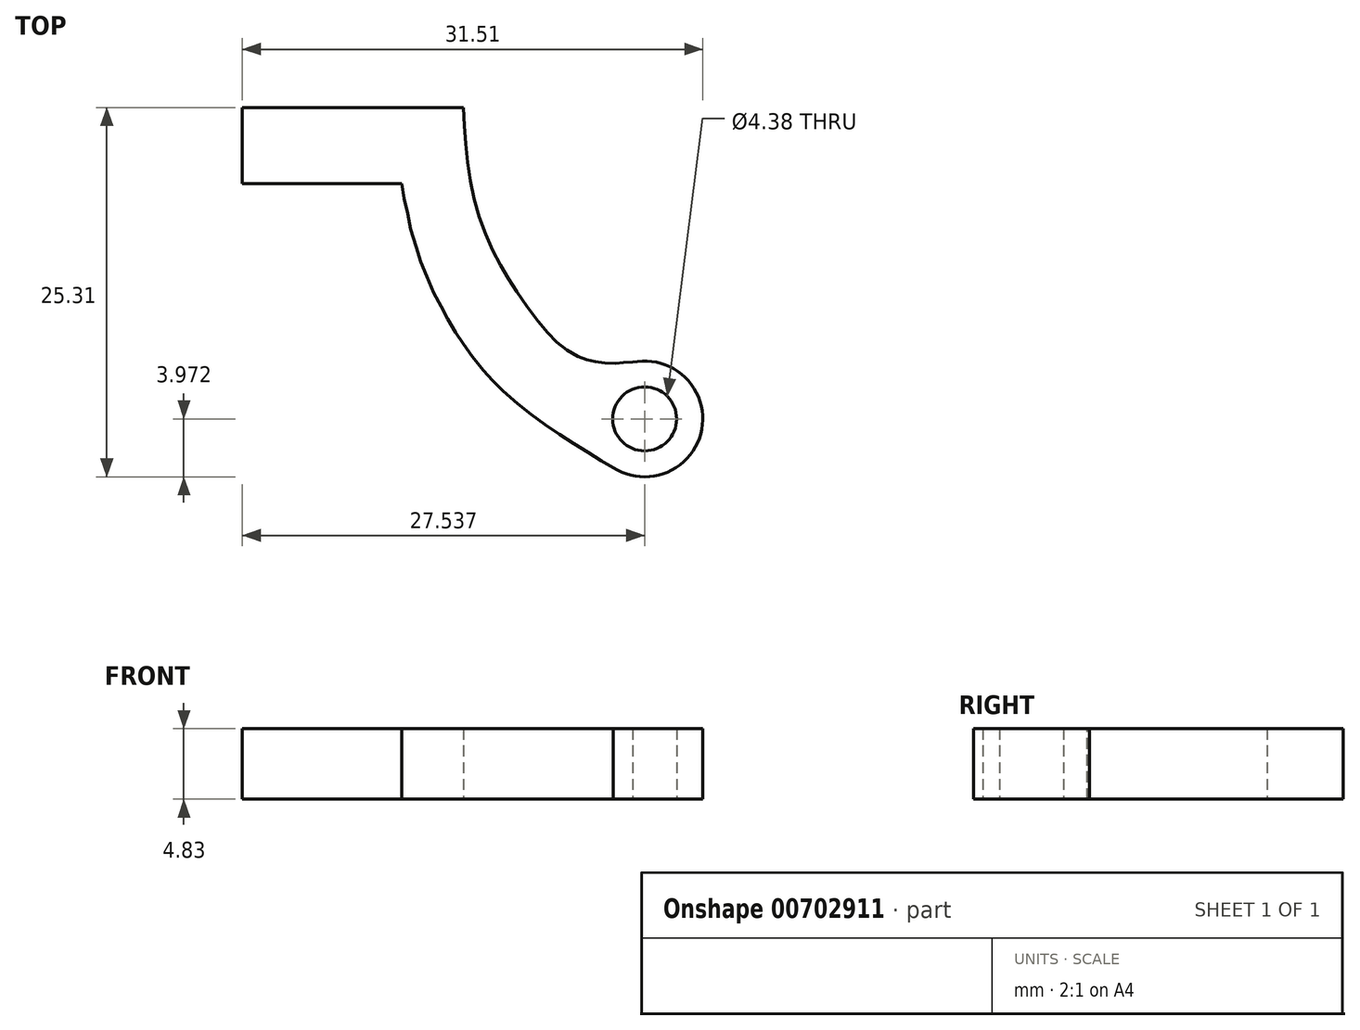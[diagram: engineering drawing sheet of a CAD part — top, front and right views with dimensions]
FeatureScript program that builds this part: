
annotation { "Feature Type Name" : "Feature", "Feature Type Description" : "" }
export const myFeature = defineFeature(function(context is Context, id is Id, definition is map)
    precondition{}
    {
        {
            var Q0;
            Q0=qCreatedBy(makeId("Top.planeOp"),FACE);
            var sketch = newSketch(context, id + "F0", { "sketchPlane" : qUnion([Q0])});
            skCircle(sketch, "E0", {"center": v(26.2, -11.99) * mm, "radius": 2.2 * mm});
            skArc(sketch, "E1", {"start": v(24.06, -15.33) * mm, "mid": v(30.11, -12.7) * mm, "end": v(25.38, -8.1) * mm});
            skLineSegment(sketch, "E2", {"start": v(-1.33, 9.35) * mm, "end": v(13.8, 9.35) * mm});
            skLineSegment(sketch, "E3", {"start": v(-1.33, 9.35) * mm, "end": v(-1.33, 4.13) * mm});
            skLineSegment(sketch, "E4", {"start": v(-1.33, 4.13) * mm, "end": v(9.6, 4.13) * mm});
            skFitSpline(sketch, "E5", {"points": [v(13.8, 9.35) * mm, v(13.95, 6.96) * mm, v(14.25, 4.44) * mm, v(14.82, 2.05) * mm, v(15.7, -0.2) * mm, v(16.6, -1.92) * mm, v(17.55, -3.41) * mm, v(18.98, -5.38) * mm, v(19.94, -6.46) * mm, v(20.8, -7.22) * mm, v(21.81, -7.78) * mm, v(22.31, -7.95) * mm, v(22.89, -8.08) * mm, v(23.6, -8.16) * mm, v(24.34, -8.18) * mm, v(24.75, -8.13) * mm, v(25.38, -8.1) * mm], "startDerivative": vector(1.35, -28.19) * mm, "endDerivative": vector(13.52, -1.17) * mm});
            skFitSpline(sketch, "E6", {"points": [v(9.6, 4.13) * mm, v(9.73, 3.17) * mm, v(9.97, 2.13) * mm, v(10.16, 1.16) * mm, v(10.57, -0.23) * mm, v(10.89, -1.25) * mm, v(11.3, -2.28) * mm, v(11.85, -3.52) * mm, v(12.32, -4.39) * mm, v(12.73, -5.16) * mm, v(13.26, -6.05) * mm, v(13.74, -6.76) * mm, v(14.24, -7.48) * mm, v(15.1, -8.6) * mm, v(15.7, -9.26) * mm, v(16.15, -9.7) * mm, v(17.27, -10.75) * mm, v(18.3, -11.59) * mm, v(19.32, -12.34) * mm, v(20.44, -13.1) * mm, v(21.46, -13.75) * mm, v(22.5, -14.4) * mm, v(23.3, -14.9) * mm, v(24.06, -15.33) * mm], "startDerivative": vector(2.7, -23.05) * mm, "endDerivative": vector(19.55, -10.87) * mm});
            skSolve(sketch);
        }
        {
            var Q0;
            Q0=makeQuery(id+"F0.imprint","IMPRINT",FACE,{"disambiguationData":[TD([[makeQuery(id+"F0.imprint","IMPRINT",EDGE,{"derivedFrom":sQuery(id+"F0.wireOp",EDGE,"E0")}),-1.0]])]});
            extrude(context, id + "F1", {"entities" : qUnion([Q0]), "depth" : 4.83 * mm, "offsetDistance" : 25.4 * mm});
        }
    });
